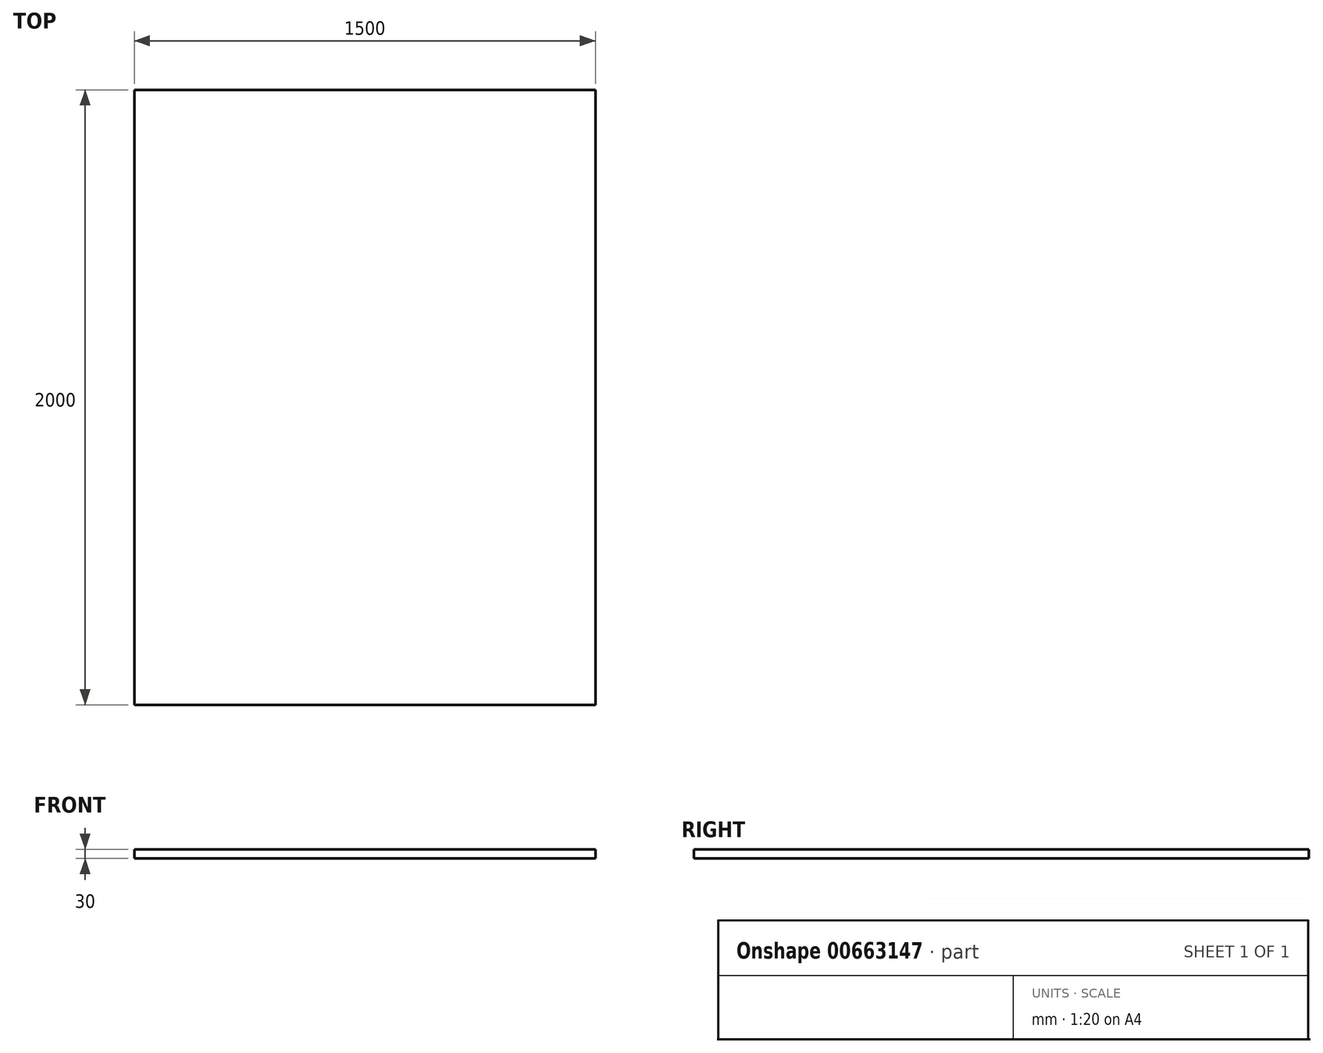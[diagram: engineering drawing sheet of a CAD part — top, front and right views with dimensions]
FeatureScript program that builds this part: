
annotation { "Feature Type Name" : "Feature", "Feature Type Description" : "" }
export const myFeature = defineFeature(function(context is Context, id is Id, definition is map)
    precondition{}
    {
        {
            var Q0;
            Q0=qCreatedBy(makeId("Front.planeOp"),FACE);
            var sketch = newSketch(context, id + "F0", { "sketchPlane" : qUnion([Q0])});
            skLineSegment(sketch, "E0.bottom", {"start": v(-99.34, 68.28) * mm, "end": v(1400.66, 68.28) * mm});
            skLineSegment(sketch, "E0.top", {"start": v(-99.34, 38.28) * mm, "end": v(1400.66, 38.28) * mm});
            skLineSegment(sketch, "E0.left", {"start": v(-99.34, 68.28) * mm, "end": v(-99.34, 38.28) * mm});
            skLineSegment(sketch, "E0.right", {"start": v(1400.66, 68.28) * mm, "end": v(1400.66, 38.28) * mm});
            skSolve(sketch);
        }
        {
            var Q0;
            Q0 = qSketchRegion(id + "F0", true);
            extrude(context, id + "F1", {"entities" : qUnion([Q0]), "depth" : 2000 * mm, "offsetDistance" : 25 * mm});
        }
    });
